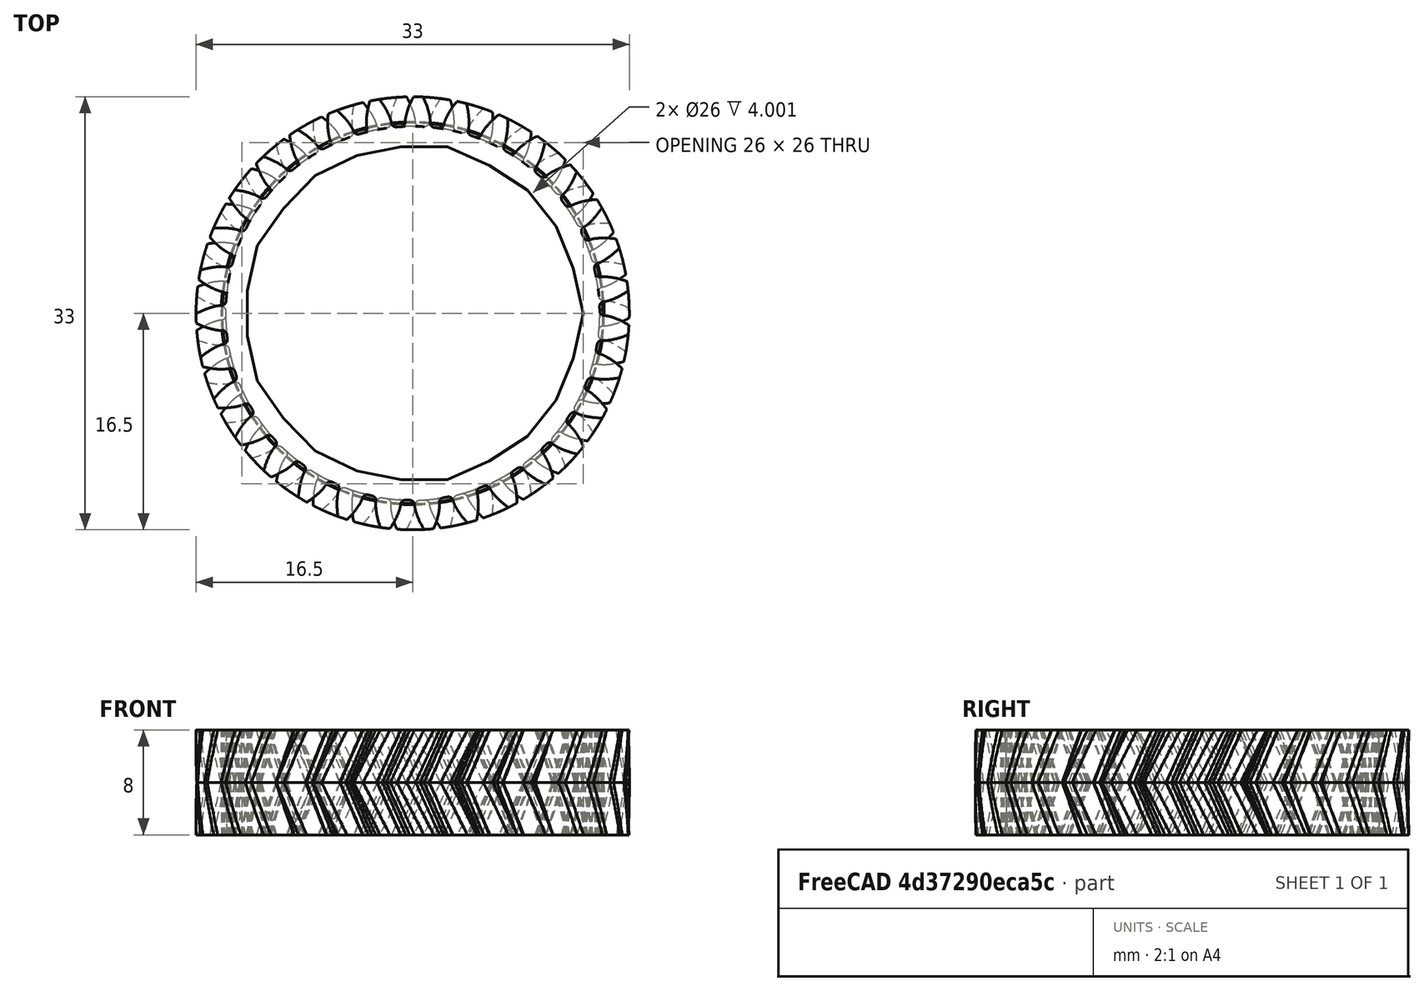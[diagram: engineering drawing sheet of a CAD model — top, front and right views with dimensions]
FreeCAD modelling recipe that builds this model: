
FCSTD DOCUMENT  (FreeCAD 0.17R13541 (Git))
Label: Gear5c
License: All rights reserved
LicenseURL: http://en.wikipedia.org/wiki/All_rights_reserved
objects: Part::Helix×2, Part::Sweep×2, Part::Cylinder×2, Part::Cut×2, Part::Part2DObjectPython×1, Part::Fuse×1
note: 10 computed .brp shape members not serialized (recipe doc carries the construction recipe); baked Part::Feature solids carry a one-line shape summary decoded from their .brp

FEATURE [Part::Part2DObjectPython] InvoluteGear  # Draft 2D object (typed FeaturePython)
  ExternalGear = true
  HighPrecision = true
  Modules = 1
  NumberOfTeeth = 31
  PressureAngle = 20
FEATURE [Part::Helix] Helix002
  Angle = 0
  AttacherType = Attacher::AttachEngine3D
  Height = 4
  LocalCoord = 0
  Pitch = 200
  Radius = 16.5
  Style = 1
FEATURE [Part::Sweep] Sweep
  Frenet = true
  Sections = -> [InvoluteGear]
  Solid = true
  Spine = -> Helix002 [Edge1]
  Transition = 1
FEATURE [Part::Helix] Helix
  Angle = 0
  AttacherType = Attacher::AttachEngine3D
  Height = 4
  LocalCoord = 1
  Pitch = 200
  Placement = pos=(0,0,0) rot=(1,0,0;3.14159rad)
  Radius = 16.5
  Style = 1
FEATURE [Part::Sweep] Sweep001
  Frenet = true
  Sections = -> [InvoluteGear]
  Solid = true
  Spine = -> Helix [Edge1]
  Transition = 1
FEATURE [Part::Cylinder] Cylinder
  Angle = 360
  AttacherType = Attacher::AttachEngine3D
  Height = 4.01
  Radius = 13
FEATURE [Part::Cylinder] Cylinder001
  Angle = 360
  AttacherType = Attacher::AttachEngine3D
  Height = 4.01
  Placement = pos=(0,0,0) rot=(1,0,0;3.14159rad)
  Radius = 13
FEATURE [Part::Cut] Cut
  Base = -> Sweep
  Tool = -> Cylinder
FEATURE [Part::Cut] Cut001
  Base = -> Sweep001
  Tool = -> Cylinder001
FEATURE [Part::Fuse] Fusion
  Base = -> Cut
  Tool = -> Cut001
